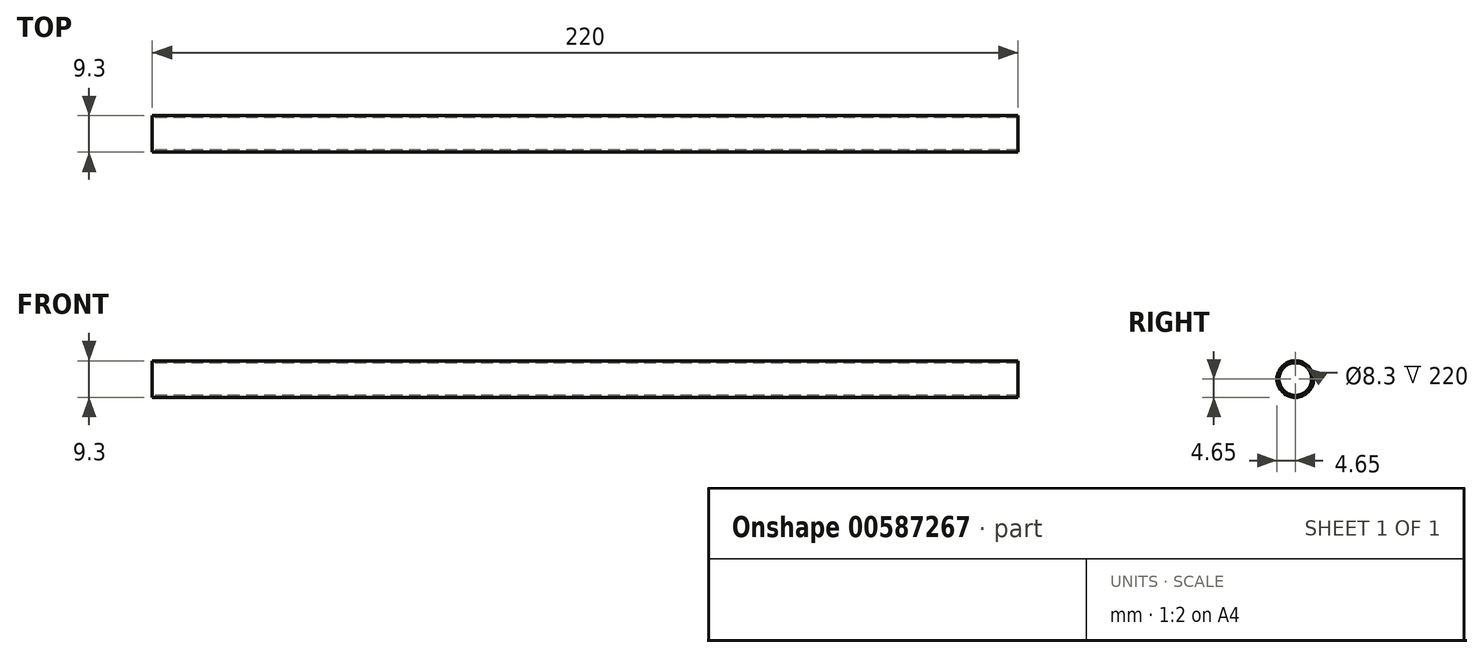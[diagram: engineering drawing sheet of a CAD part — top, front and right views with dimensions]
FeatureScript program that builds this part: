
annotation { "Feature Type Name" : "Feature", "Feature Type Description" : "" }
export const myFeature = defineFeature(function(context is Context, id is Id, definition is map)
    precondition{}
    {
        {
            var Q0;
            Q0=qCreatedBy(makeId("Right.planeOp"),FACE);
            var sketch = newSketch(context, id + "F0", { "sketchPlane" : qUnion([Q0])});
            skCircle(sketch, "E0", {"center": v(0, 0) * mm, "radius": 4.65 * mm});
            skSolve(sketch);
        }
        {
            var Q0;
            Q0=makeQuery(id+"F0.imprint","IMPRINT",FACE,{"disambiguationData":[TD([[makeQuery(id+"F0.imprint","IMPRINT",EDGE,{"derivedFrom":sQuery(id+"F0.wireOp",EDGE,"E0")}),1.0]])]});
            extrude(context, id + "F1", {"entities" : qUnion([Q0]), "depth" : 110 * mm, "offsetDistance" : 25 * mm, "hasSecondDirection" : true, "secondDirectionOppositeDirection" : true, "secondDirectionDepth" : 110 * mm});
        }
        {
            var Q0;
            Q0=makeQuery(id+"F1.opExtrude","CAP_FACE",FACE,{"disambiguationData":[OSD([sQuery(id+"F0.wireOp",EDGE,"E0")])],"isStart":false});
            var Q1;
            Q1=makeQuery(id+"F1.opExtrude","CAP_FACE",FACE,{"disambiguationData":[OSD([sQuery(id+"F0.wireOp",EDGE,"E0")])],"isStart":true});
            var Q2;
            Q2=makeQuery(id+"F1.opExtrude","SWEPT_BODY",BODY,{"disambiguationData":[OSD([sQuery(id+"F0.wireOp",EDGE,"E0")])]});
            shell(context, id + "F2", {"entities" : qUnion([Q0, Q1]), "parts" : qUnion([Q2]), "thickness" : .5 * mm});
        }
    });
